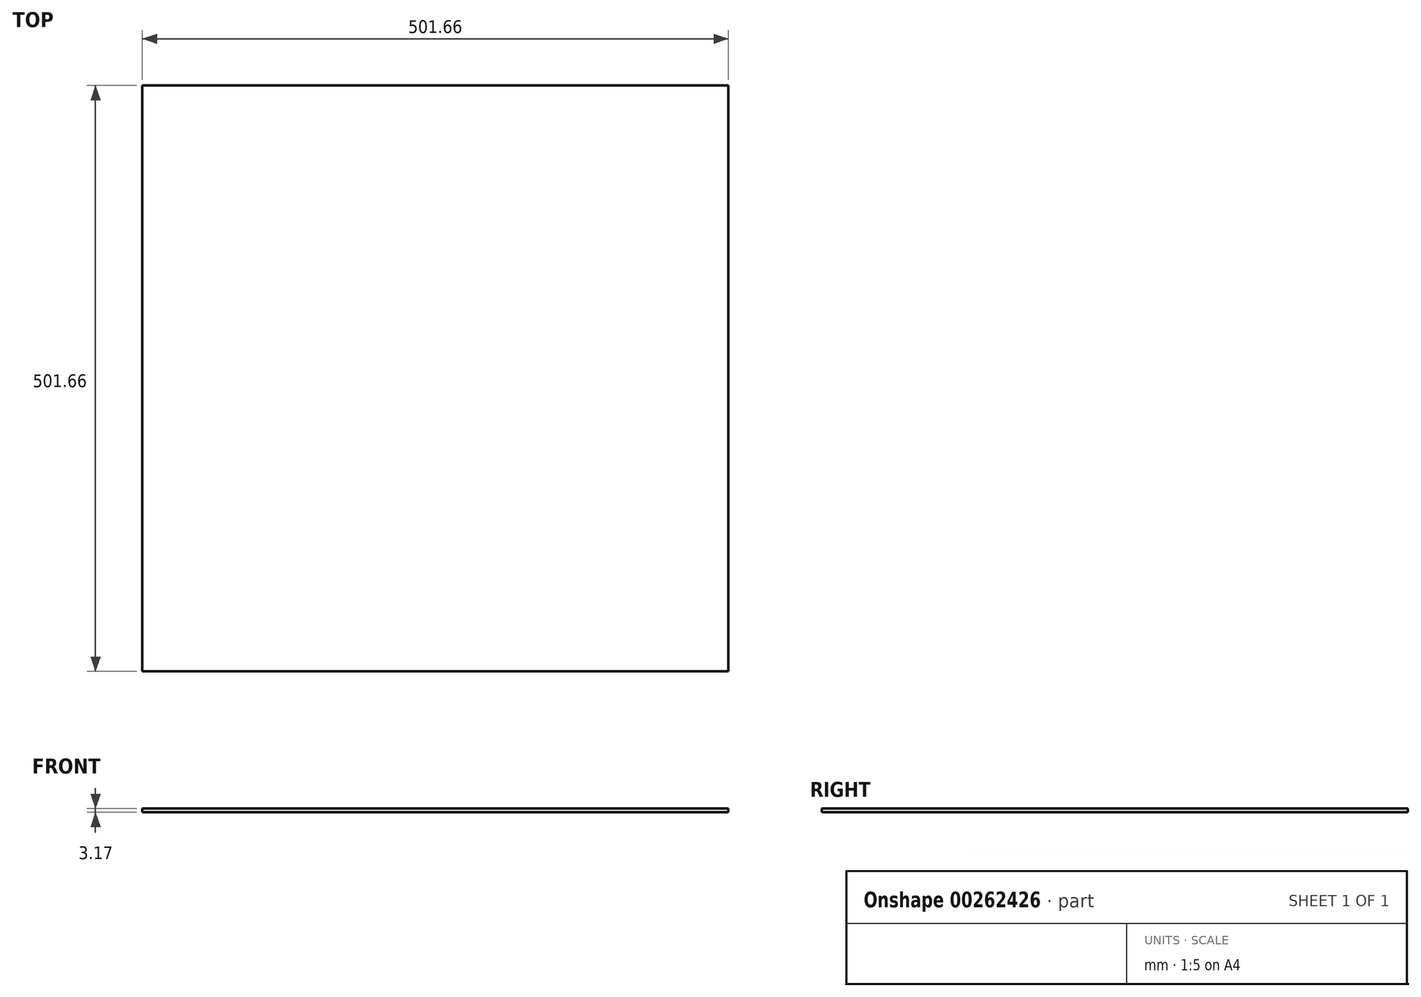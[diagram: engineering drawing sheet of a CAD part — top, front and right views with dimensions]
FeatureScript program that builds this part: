
annotation { "Feature Type Name" : "Feature", "Feature Type Description" : "" }
export const myFeature = defineFeature(function(context is Context, id is Id, definition is map)
    precondition{}
    {
        {
            var Q0;
            Q0=qCreatedBy(makeId("Top.planeOp"),FACE);
            var sketch = newSketch(context, id + "F0", { "sketchPlane" : qUnion([Q0])});
            skLineSegment(sketch, "E0.bottom", {"start": v(250.83, 250.82) * mm, "end": v(-250.83, 250.82) * mm});
            skLineSegment(sketch, "E0.top", {"start": v(250.83, -250.83) * mm, "end": v(-250.83, -250.83) * mm});
            skLineSegment(sketch, "E0.left", {"start": v(250.83, 250.83) * mm, "end": v(250.83, -250.83) * mm});
            skLineSegment(sketch, "E0.right", {"start": v(-250.83, 250.83) * mm, "end": v(-250.83, -250.83) * mm});
            skPoint(sketch, "E0.middle", {"position": v(0, 0) * mm});
            skSolve(sketch);
        }
        {
            var Q0;
            Q0 = qSketchRegion(id + "F0", true);
            extrude(context, id + "F1", {"entities" : qUnion([Q0]), "depth" : 3.17 * mm});
        }
    });
